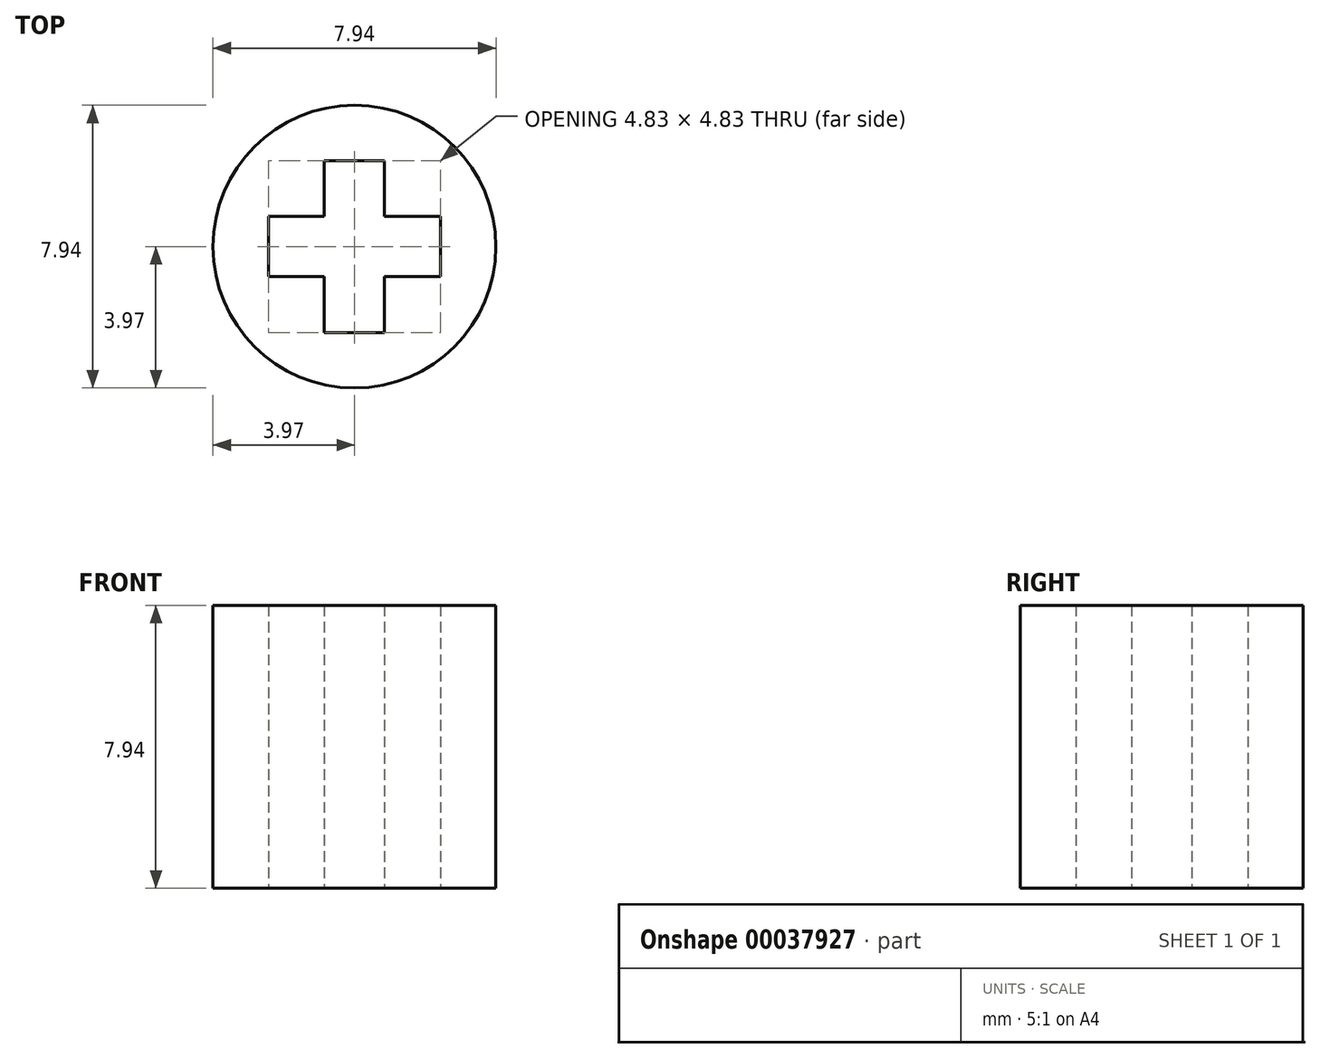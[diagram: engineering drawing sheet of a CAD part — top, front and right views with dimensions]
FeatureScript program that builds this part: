
annotation { "Feature Type Name" : "Feature", "Feature Type Description" : "" }
export const myFeature = defineFeature(function(context is Context, id is Id, definition is map)
    precondition{}
    {
        {
            var Q0;
            Q0=qCreatedBy(makeId("Top.planeOp"),FACE);
            var sketch = newSketch(context, id + "F0", { "sketchPlane" : qUnion([Q0])});
            skCircle(sketch, "E0", {"center": v(0, 0) * mm, "radius": 3.97 * mm});
            skLineSegment(sketch, "E1.rect.bottom", {"start": v(2.41, 0.84) * mm, "end": v(-2.41, 0.84) * mm});
            skLineSegment(sketch, "E1.rect.top", {"start": v(2.41, -0.84) * mm, "end": v(-2.41, -0.84) * mm});
            skLineSegment(sketch, "E1.rect.left", {"start": v(2.41, 0.84) * mm, "end": v(2.41, -0.84) * mm});
            skLineSegment(sketch, "E1.rect.right", {"start": v(-2.41, 0.84) * mm, "end": v(-2.41, -0.84) * mm});
            skLineSegment(sketch, "E2.rect.bottom", {"start": v(0.84, -2.41) * mm, "end": v(-0.84, -2.41) * mm});
            skLineSegment(sketch, "E2.rect.top", {"start": v(0.84, 2.41) * mm, "end": v(-0.84, 2.41) * mm});
            skLineSegment(sketch, "E2.rect.left", {"start": v(0.84, -2.41) * mm, "end": v(0.84, 2.41) * mm});
            skLineSegment(sketch, "E2.rect.right", {"start": v(-0.84, -2.41) * mm, "end": v(-0.84, 2.41) * mm});
            skSolve(sketch);
        }
        {
            var Q0;
            Q0=qSketchRegion(id+"F0",true);
            extrude(context, id + "F1", {"entities" : qUnion([Q0]), "depth" : 7.94 * mm});
        }
    });
